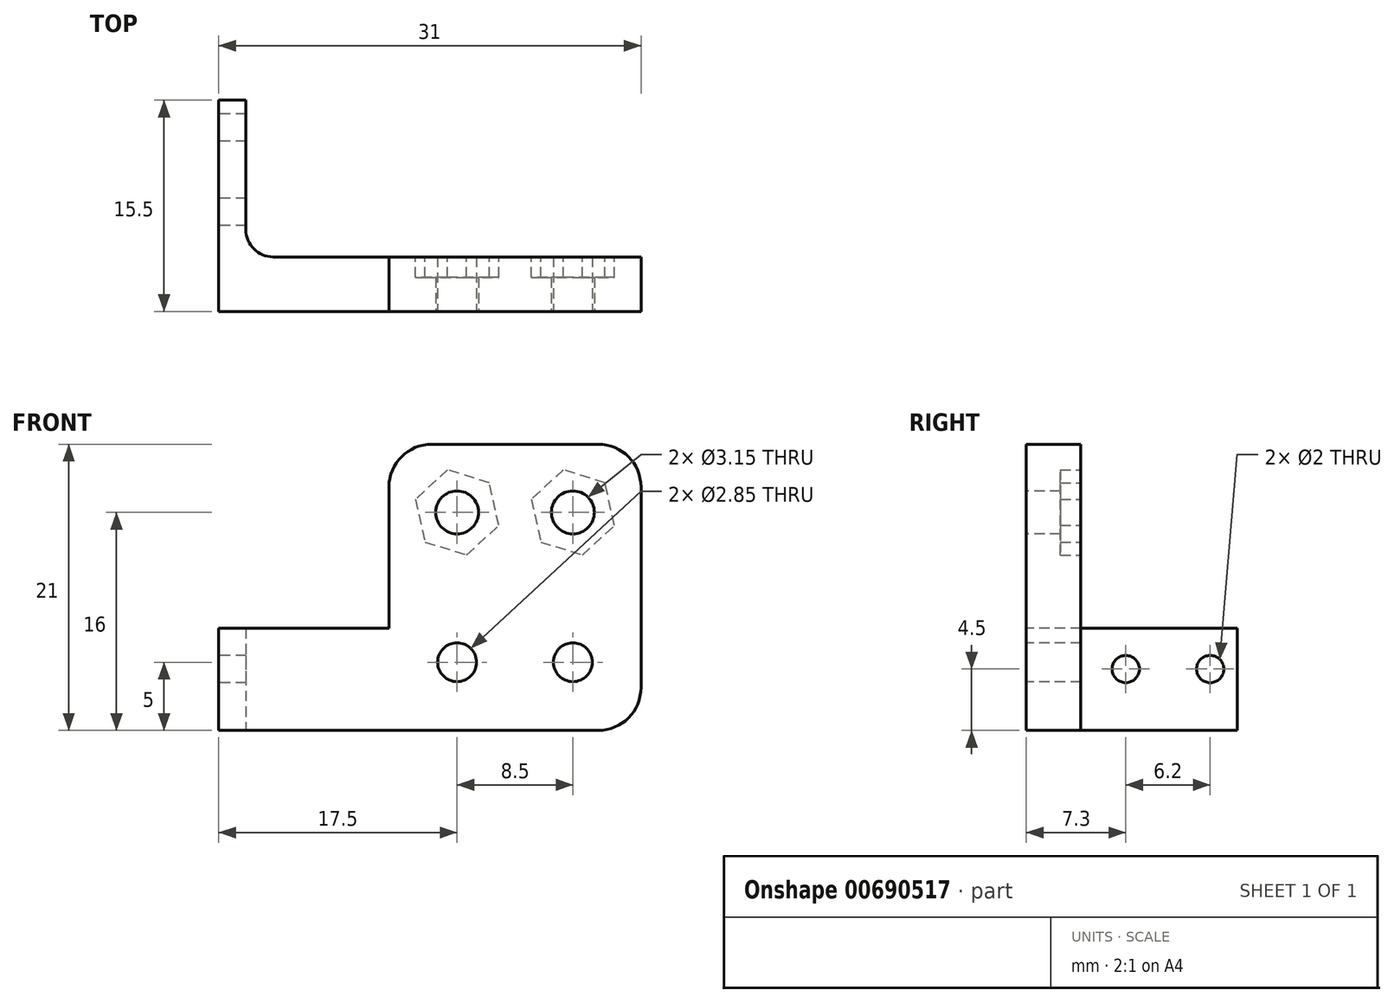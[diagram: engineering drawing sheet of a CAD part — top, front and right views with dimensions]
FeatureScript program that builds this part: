
annotation { "Feature Type Name" : "Feature", "Feature Type Description" : "" }
export const myFeature = defineFeature(function(context is Context, id is Id, definition is map)
    precondition{}
    {
        {
            var Q0;
            Q0=qCreatedBy(makeId("Front.planeOp"),FACE);
            var sketch = newSketch(context, id + "F0", { "sketchPlane" : qUnion([Q0])});
            skLineSegment(sketch, "E0", {"start": v(-13.5, 13.5) * mm, "end": v(-13.5, -7.5) * mm});
            skLineSegment(sketch, "E1", {"start": v(-13.5, -7.5) * mm, "end": v(5, -7.5) * mm});
            skLineSegment(sketch, "E2", {"start": v(5, -7.5) * mm, "end": v(5, 13.5) * mm});
            skLineSegment(sketch, "E3", {"start": v(5, 13.5) * mm, "end": v(-13.5, 13.5) * mm});
            skCircle(sketch, "E4", {"center": v(0, 8.5) * mm, "radius": 1.57 * mm});
            skCircle(sketch, "E5", {"center": v(-8.5, 8.5) * mm, "radius": 1.57 * mm});
            skCircle(sketch, "E6", {"center": v(-8.5, -2.5) * mm, "radius": 1.43 * mm});
            skCircle(sketch, "E7", {"center": v(0, -2.5) * mm, "radius": 1.43 * mm});
            skLineSegment(sketch, "E8", {"start": v(-13.5, 0) * mm, "end": v(-26, 0) * mm});
            skLineSegment(sketch, "E9", {"start": v(-13.5, -7.5) * mm, "end": v(-26, -7.5) * mm});
            skLineSegment(sketch, "E10", {"start": v(-26, -7.5) * mm, "end": v(-26, 0) * mm});
            skLineSegment(sketch, "E11", {"start": v(-24, 0) * mm, "end": v(-24, -7.5) * mm});
            skSolve(sketch);
        }
        {
            var Q0;
            Q0=makeQuery(id+"F0.imprint","IMPRINT",FACE,{"disambiguationData":[TD([[makeQuery(id+"F0.imprint","IMPRINT",EDGE,{"derivedFrom":sQuery(id+"F0.wireOp",EDGE,"E0")}),1.0]])]});
            extrude(context, id + "F1", {"entities" : qUnion([Q0]), "oppositeDirection" : true, "depth" : 4 * mm, "offsetDistance" : 25 * mm});
        }
        {
            var Q0;
            Q0=makeQuery(id+"F1.opExtrude","CAP_FACE",FACE,{"disambiguationData":[OSD([sQuery(id+"F0.wireOp",EDGE,"E0"),sQuery(id+"F0.wireOp",EDGE,"E1"),sQuery(id+"F0.wireOp",EDGE,"E2"),sQuery(id+"F0.wireOp",EDGE,"E3"),sQuery(id+"F0.wireOp",EDGE,"E4"),sQuery(id+"F0.wireOp",EDGE,"E5"),sQuery(id+"F0.wireOp",EDGE,"E6"),sQuery(id+"F0.wireOp",EDGE,"E7")])],"isStart":false});
            var sketch = newSketch(context, id + "F2", { "sketchPlane" : qUnion([Q0])});
            skCircle(sketch, "E12.cCircle", {"center": v(0, 8.5) * mm, "radius": 2.77 * mm, "construction": true});
            skLineSegment(sketch, "E12.0", {"start": v(2.36, 6.33) * mm, "end": v(-0.7, 5.37) * mm});
            skLineSegment(sketch, "E12.1", {"start": v(-0.7, 5.37) * mm, "end": v(-3.06, 7.54) * mm});
            skLineSegment(sketch, "E12.2", {"start": v(-3.06, 7.54) * mm, "end": v(-2.36, 10.67) * mm});
            skLineSegment(sketch, "E12.3", {"start": v(-2.36, 10.67) * mm, "end": v(0.7, 11.63) * mm});
            skLineSegment(sketch, "E12.4", {"start": v(0.7, 11.63) * mm, "end": v(3.06, 9.46) * mm});
            skLineSegment(sketch, "E12.5", {"start": v(3.06, 9.46) * mm, "end": v(2.36, 6.33) * mm});
            skPoint(sketch, "E12.0.midPoint", {"position": v(0.83, 5.85) * mm});
            skCircle(sketch, "E13.cCircle", {"center": v(8.5, 8.5) * mm, "radius": 2.77 * mm, "construction": true});
            skLineSegment(sketch, "E13.0", {"start": v(10.86, 6.33) * mm, "end": v(7.8, 5.37) * mm});
            skLineSegment(sketch, "E13.1", {"start": v(7.8, 5.37) * mm, "end": v(5.44, 7.54) * mm});
            skLineSegment(sketch, "E13.2", {"start": v(5.44, 7.54) * mm, "end": v(6.14, 10.67) * mm});
            skLineSegment(sketch, "E13.3", {"start": v(6.14, 10.67) * mm, "end": v(9.2, 11.63) * mm});
            skLineSegment(sketch, "E13.4", {"start": v(9.2, 11.63) * mm, "end": v(11.56, 9.46) * mm});
            skLineSegment(sketch, "E13.5", {"start": v(11.56, 9.46) * mm, "end": v(10.86, 6.33) * mm});
            skPoint(sketch, "E13.0.midPoint", {"position": v(9.33, 5.85) * mm});
            skSolve(sketch);
        }
        {
            var Q0;
            Q0 = qSketchRegion(id + "F2", true);
            extrude(context, id + "F3", {"entities" : qUnion([Q0]), "operationType" : NewBodyOperationType.REMOVE, "oppositeDirection" : true, "depth" : 1.5 * mm, "offsetDistance" : 25 * mm});
        }
        {
            var Q0;
            Q0=makeQuery(id+"F1.opExtrude","SWEPT_EDGE",EDGE,{"disambiguationData":[OSD([sQuery(id+"F0.wireOp",EDGE,"E2"),sQuery(id+"F0.wireOp",EDGE,"E3")])]});
            var Q1;
            Q1=makeQuery(id+"F1.opExtrude","SWEPT_EDGE",EDGE,{"disambiguationData":[OSD([sQuery(id+"F0.wireOp",EDGE,"E0"),sQuery(id+"F0.wireOp",EDGE,"E3")])]});
            var Q2;
            Q2=makeQuery(id+"F1.opExtrude","SWEPT_EDGE",EDGE,{"disambiguationData":[OSD([sQuery(id+"F0.wireOp",EDGE,"E1"),sQuery(id+"F0.wireOp",EDGE,"E2")])]});
            fillet(context, id + "F4", {"entities" : qUnion([Q0, Q1, Q2]), "radius" : 3.14 * mm, "tangentPropagation" : true, "allowEdgeOverflow" : false});
        }
        {
            var Q0;
            {var subQ0=sQuery(id+"F0.wireOp",EDGE,"E10");Q0=makeQuery(id+"F0.imprint","IMPRINT",FACE,{"disambiguationData":[TD([[makeQuery(id+"F0.imprint","IMPRINT",EDGE,{"derivedFrom":subQ0}),-1.0]])]});}
            var Q1;
            {var subQ5=sQuery(id+"F0.wireOp",EDGE,"E11");Q1=makeQuery(id+"F0.imprint","IMPRINT",FACE,{"disambiguationData":[TD([[makeQuery(id+"F0.imprint","IMPRINT",EDGE,{"derivedFrom":subQ5}),1.0]])]});}
            extrude(context, id + "F5", {"entities" : qUnion([Q0, Q1]), "operationType" : NewBodyOperationType.ADD, "oppositeDirection" : true, "depth" : 4 * mm, "offsetDistance" : 25 * mm});
        }
        {
            var Q0;
            {var subQ0=sQuery(id+"F0.wireOp",EDGE,"E10");Q0=makeQuery(id+"F0.imprint","IMPRINT",FACE,{"disambiguationData":[TD([[makeQuery(id+"F0.imprint","IMPRINT",EDGE,{"derivedFrom":subQ0}),-1.0]])]});}
            extrude(context, id + "F6", {"entities" : qUnion([Q0]), "operationType" : NewBodyOperationType.ADD, "oppositeDirection" : true, "depth" : 15.5 * mm, "offsetDistance" : 25 * mm});
        }
        {
            var Q0;
            {var subQ0=sQuery(id+"F0.wireOp",EDGE,"E10");Q0=makeQuery(id+"F6.boolean.opBoolean","MERGE",FACE,{"derivedFrom":[makeQuery(id+"F5.opExtrude","SWEPT_FACE",FACE,{"disambiguationData":[OSD([subQ0])]}),makeQuery(id+"F6.opExtrude","SWEPT_FACE",FACE,{"disambiguationData":[OSD([subQ0])]})]});}
            var sketch = newSketch(context, id + "F7", { "sketchPlane" : qUnion([Q0])});
            skCircle(sketch, "E14", {"center": v(-13.5, -3) * mm, "radius": 1 * mm});
            skCircle(sketch, "E15", {"center": v(-7.3, -3) * mm, "radius": 1 * mm});
            skSolve(sketch);
        }
        {
            var Q0;
            Q0=makeQuery(id+"F7.imprint","IMPRINT",FACE,{"disambiguationData":[TD([[makeQuery(id+"F7.imprint","IMPRINT",EDGE,{"derivedFrom":sQuery(id+"F7.wireOp",EDGE,"E14")}),1.0]])]});
            var Q1;
            Q1=makeQuery(id+"F7.imprint","IMPRINT",FACE,{"disambiguationData":[TD([[makeQuery(id+"F7.imprint","IMPRINT",EDGE,{"derivedFrom":sQuery(id+"F7.wireOp",EDGE,"E15")}),1.0]])]});
            extrude(context, id + "F8", {"entities" : qUnion([Q0, Q1]), "operationType" : NewBodyOperationType.REMOVE, "oppositeDirection" : true, "depth" : 3 * mm, "offsetDistance" : 25 * mm});
        }
        {
            var Q0;
            {var subQ0=sQuery(id+"F0.wireOp",EDGE,"E0");Q0=makeQuery(id+"F6.boolean.opBoolean","INTERSECT",EDGE,{"derivedFrom":[makeQuery(id+"F5.boolean.opBoolean","MERGE",FACE,{"derivedFrom":[makeQuery(id+"F1.opExtrude","CAP_FACE",FACE,{"disambiguationData":[OSD([subQ0,sQuery(id+"F0.wireOp",EDGE,"E1"),sQuery(id+"F0.wireOp",EDGE,"E2"),sQuery(id+"F0.wireOp",EDGE,"E3"),sQuery(id+"F0.wireOp",EDGE,"E4"),sQuery(id+"F0.wireOp",EDGE,"E5"),sQuery(id+"F0.wireOp",EDGE,"E6"),sQuery(id+"F0.wireOp",EDGE,"E7")])],"isStart":false}),makeQuery(id+"F5.opExtrude","CAP_FACE",FACE,{"disambiguationData":[OSD([subQ0,sQuery(id+"F0.wireOp",EDGE,"E8"),sQuery(id+"F0.wireOp",EDGE,"E9"),sQuery(id+"F0.wireOp",EDGE,"E10")])],"isStart":false})]}),makeQuery(id+"F6.opExtrude","SWEPT_FACE",FACE,{"disambiguationData":[OSD([sQuery(id+"F0.wireOp",EDGE,"E11")])]})]});}
            fillet(context, id + "F9", {"entities" : qUnion([Q0]), "radius" : 2 * mm, "tangentPropagation" : true, "allowEdgeOverflow" : false});
        }
    });
